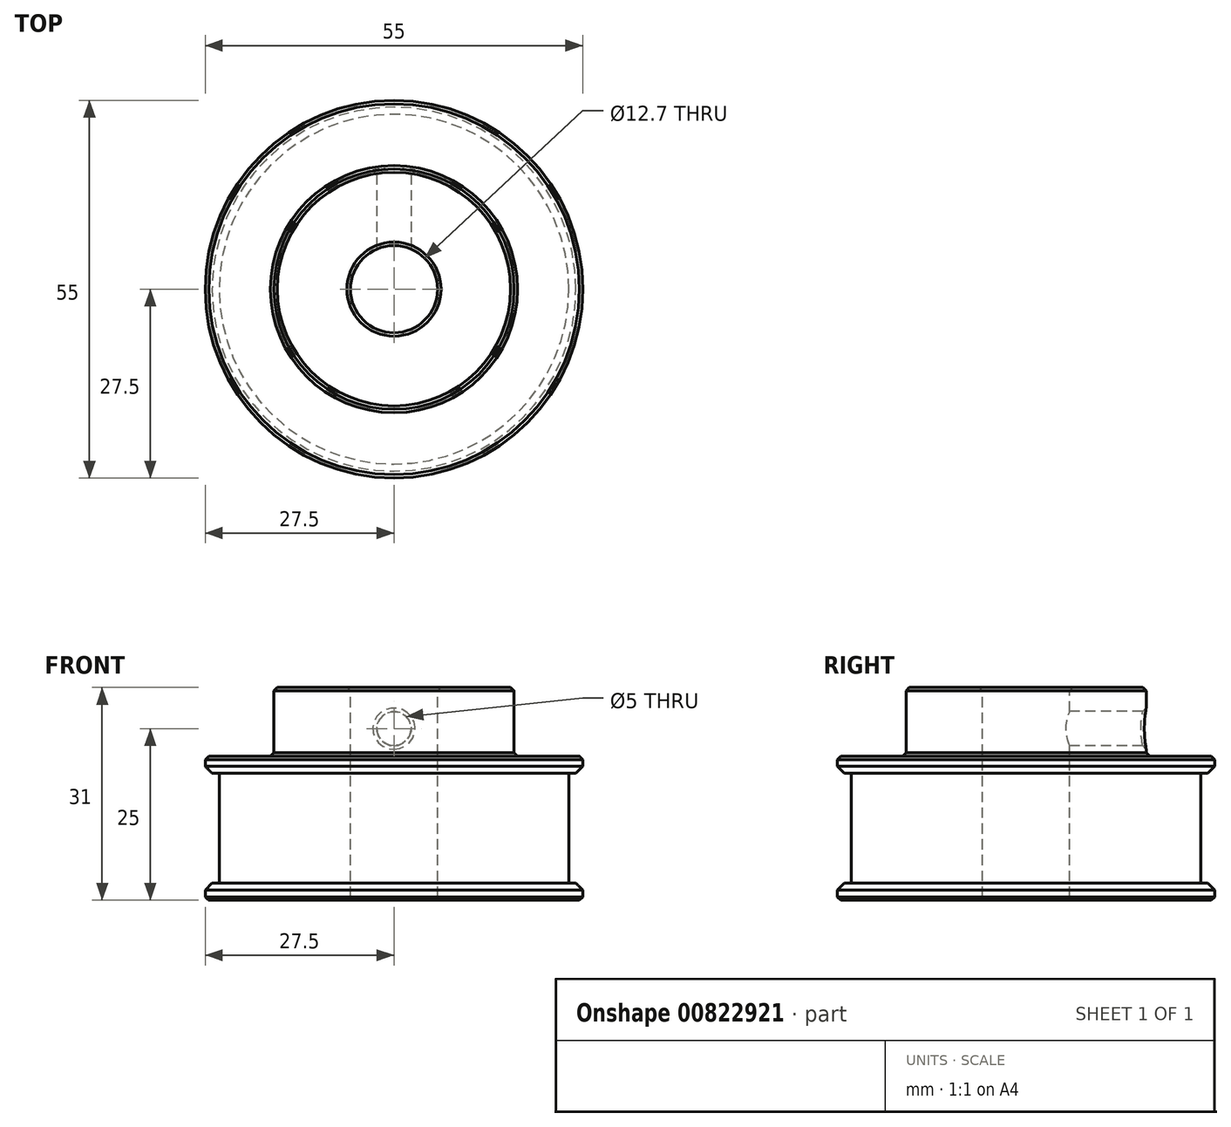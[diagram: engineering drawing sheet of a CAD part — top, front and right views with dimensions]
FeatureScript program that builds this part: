
annotation { "Feature Type Name" : "Feature", "Feature Type Description" : "" }
export const myFeature = defineFeature(function(context is Context, id is Id, definition is map)
    precondition{}
    {
        {
            var Q0;
            Q0=qCreatedBy(makeId("Front.planeOp"),FACE);
            var sketch = newSketch(context, id + "F0", { "sketchPlane" : qUnion([Q0])});
            skLineSegment(sketch, "E0", {"start": v(0, 38.23) * mm, "end": v(0, 0) * mm, "construction": true});
            skLineSegment(sketch, "E1", {"start": v(0, 0) * mm, "end": v(-6.35, 0) * mm, "construction": true});
            skLineSegment(sketch, "E2", {"start": v(-6.35, 0) * mm, "end": v(-6.35, 31) * mm});
            skLineSegment(sketch, "E3", {"start": v(-6.35, 31) * mm, "end": v(-17.5, 31) * mm});
            skLineSegment(sketch, "E4", {"start": v(-17.5, 31) * mm, "end": v(-17.5, 21) * mm});
            skLineSegment(sketch, "E5", {"start": v(-17.5, 21) * mm, "end": v(-27.5, 21) * mm});
            skLineSegment(sketch, "E6", {"start": v(-27.5, 21) * mm, "end": v(-27.5, 18.5) * mm});
            skLineSegment(sketch, "E7", {"start": v(-27.5, 18.5) * mm, "end": v(-25.46, 18.5) * mm});
            skLineSegment(sketch, "E8", {"start": v(-25.46, 18.5) * mm, "end": v(-25.46, 2.5) * mm});
            skLineSegment(sketch, "E9", {"start": v(-25.46, 2.5) * mm, "end": v(-27.5, 2.5) * mm});
            skLineSegment(sketch, "E10", {"start": v(-27.5, 2.5) * mm, "end": v(-27.5, 0) * mm});
            skLineSegment(sketch, "E11", {"start": v(-27.5, 0) * mm, "end": v(-6.35, 0) * mm});
            skSolve(sketch);
        }
        {
            var Q0;
            Q0=qSketchRegion(id+"F0",true);
            var Q1;
            Q1=sQuery(id+"F0.wireOp",EDGE,"E0");
            revolve(context, id + "F1", {"surfaceOperationType" : NewSurfaceOperationType.NEW, "entities" : qUnion([Q0]), "axis" : qUnion([Q1]), "revolveType" : RevolveType.FULL});
        }
        {
            var Q0;
            Q0=makeQuery(id+"F1.opRevolve","SWEPT_EDGE",EDGE,{"disambiguationData":[OSD([sQuery(id+"F0.wireOp",EDGE,"E9"),sQuery(id+"F0.wireOp",EDGE,"E10")])]});
            var Q1;
            Q1=makeQuery(id+"F1.opRevolve","SWEPT_EDGE",EDGE,{"disambiguationData":[OSD([sQuery(id+"F0.wireOp",EDGE,"E6"),sQuery(id+"F0.wireOp",EDGE,"E7")])]});
            chamfer(context, id + "F2", {"entities" : qUnion([Q0, Q1]), "width" : 1 * mm, "tangentPropagation" : true});
        }
        {
            var Q0;
            Q0=makeQuery(id+"F1.opRevolve","SWEPT_FACE",FACE,{"disambiguationData":[OSD([sQuery(id+"F0.wireOp",EDGE,"E5")])]});
            var Q1;
            Q1=makeQuery(id+"F1.opRevolve","SWEPT_FACE",FACE,{"disambiguationData":[OSD([sQuery(id+"F0.wireOp",EDGE,"E3")])]});
            var Q2;
            Q2=makeQuery(id+"F1.opRevolve","SWEPT_FACE",FACE,{"disambiguationData":[OSD([sQuery(id+"F0.wireOp",EDGE,"E11")])]});
            chamfer(context, id + "F3", {"entities" : qUnion([Q0, Q1, Q2]), "width" : 0.5 * mm, "tangentPropagation" : true});
        }
        {
            var Q0;
            Q0=qCreatedBy(makeId("Front.planeOp"),FACE);
            var sketch = newSketch(context, id + "F4", { "sketchPlane" : qUnion([Q0])});
            skLineSegment(sketch, "E12", {"start": v(0, 0) * mm, "end": v(0, 25) * mm, "construction": true});
            skCircle(sketch, "E13", {"center": v(0, 25) * mm, "radius": 2.5 * mm});
            skSolve(sketch);
        }
        {
            var Q0;
            Q0=qSketchRegion(id+"F4",true);
            extrude(context, id + "F5", {"entities" : qUnion([Q0]), "operationType" : NewBodyOperationType.REMOVE, "oppositeDirection" : true, "depth" : 25 * mm, "offsetDistance" : 25 * mm});
        }
        {
            var Q0;
            Q0=makeQuery(id+"F5.boolean.opBoolean","INTERSECT",EDGE,{"derivedFrom":[makeQuery(id+"F1.opRevolve","SWEPT_FACE",FACE,{"disambiguationData":[OSD([sQuery(id+"F0.wireOp",EDGE,"E4")])]}),makeQuery(id+"F5.opExtrude","SWEPT_FACE",FACE,{"disambiguationData":[OSD([sQuery(id+"F4.wireOp",EDGE,"E13")])]})]});
            chamfer(context, id + "F6", {"entities" : qUnion([Q0]), "width" : 0.5 * mm, "tangentPropagation" : true});
        }
    });
